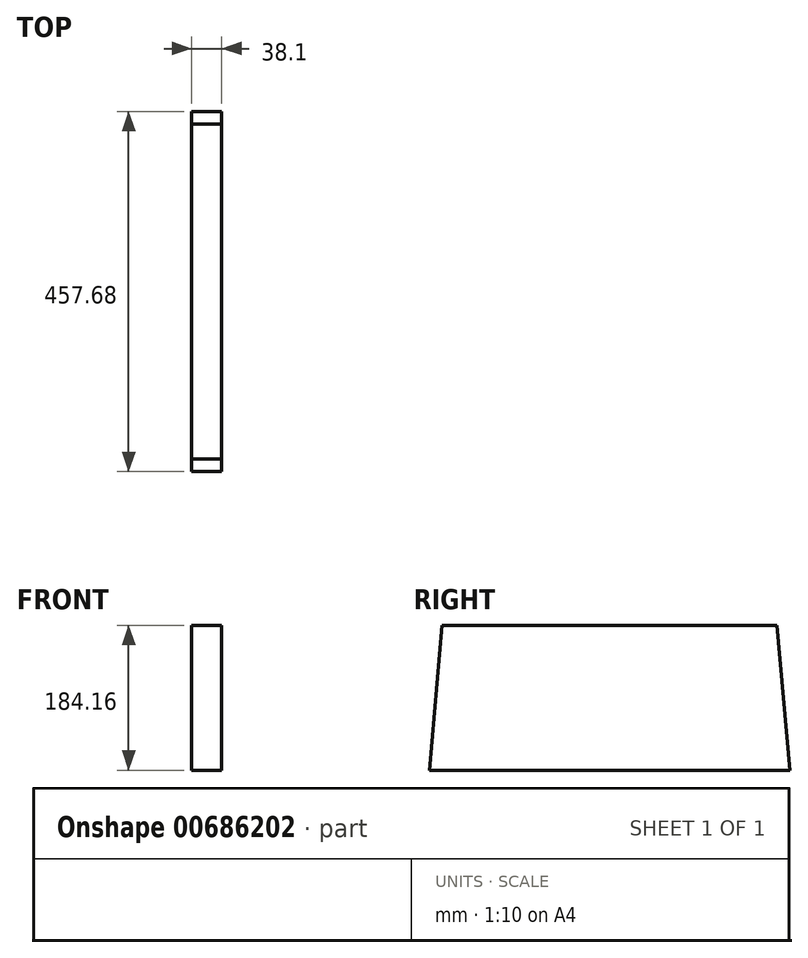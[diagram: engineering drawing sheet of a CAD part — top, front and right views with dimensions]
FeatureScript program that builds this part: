
annotation { "Feature Type Name" : "Feature", "Feature Type Description" : "" }
export const myFeature = defineFeature(function(context is Context, id is Id, definition is map)
    precondition{}
    {
        {
            var Q0;
            Q0=qCreatedBy(makeId("Right.planeOp"),FACE);
            var sketch = newSketch(context, id + "F0", { "sketchPlane" : qUnion([Q0])});
            skLineSegment(sketch, "E0.bottom", {"start": v(212.73, 92.07) * mm, "end": v(-212.72, 92.08) * mm});
            skLineSegment(sketch, "E0.top", {"start": v(228.84, -92.08) * mm, "end": v(-228.84, -92.07) * mm});
            skLineSegment(sketch, "E0.left", {"start": v(212.73, 92.07) * mm, "end": v(228.84, -92.08) * mm});
            skLineSegment(sketch, "E0.right", {"start": v(-212.73, 92.07) * mm, "end": v(-228.84, -92.08) * mm});
            skLineSegment(sketch, "E1", {"start": v(0, 0) * mm, "end": v(0, 92.07) * mm, "construction": true});
            skLineSegment(sketch, "E2", {"start": v(12.49, 0) * mm, "end": v(366.38, 0) * mm, "construction": true});
            skSolve(sketch);
        }
        {
            var Q0;
            Q0 = qSketchRegion(id + "F0", true);
            extrude(context, id + "F1", {"entities" : qUnion([Q0]), "depth" : 38.1 * mm, "offsetDistance" : 25.4 * mm});
        }
    });
